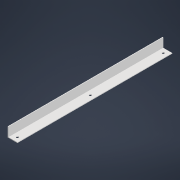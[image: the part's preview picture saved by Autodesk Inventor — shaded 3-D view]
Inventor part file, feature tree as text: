
AUTODESK INVENTOR PART (.ipt)
format: ipt  version: 2021 (Build 250183000, 183)  size: 107,520 bytes
history: native  units: mm
features: sketch x2, other x1, extrude x1, hole x1
ambient origin geometry x8: Origin, YZ Plane, XZ Plane, XY Plane, X Axis, Y Axis, Z Axis, Center Point
bodies: Body1 (feature_tree)
feature tree (5):
  other  "ソリッド1"
  extrude  "押し出し1"  Depth=10.0mm
  hole  "穴1"  [1 undecoded]
  sketch  "スケッチ2"
  sketch  "スケッチ3"
note: 1 required parameter value undecoded (feature->parameter linkage not recoverable at this tier; creation-order binding heuristic only, values carry confidence <= 0.55)
